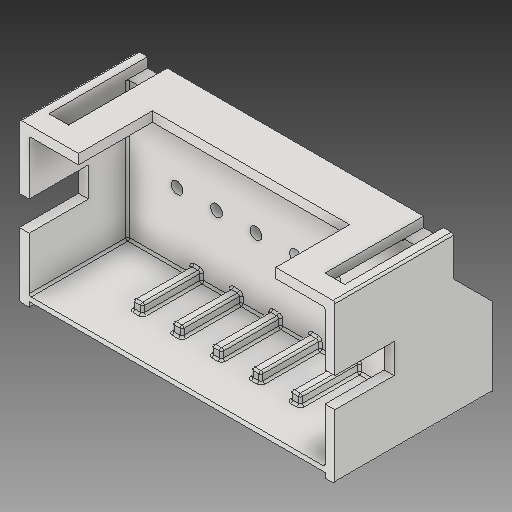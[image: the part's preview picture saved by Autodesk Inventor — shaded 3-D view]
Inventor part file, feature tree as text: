
AUTODESK INVENTOR PART (.ipt)
format: ipt  version: 2019 (Build 230136000, 136)  size: 262,656 bytes
history: mixed  units: mm
features: other x1, fillet x1, imported_body x1
ambient origin geometry x8: Origin, YZ Plane, XZ Plane, XY Plane, X Axis, Y Axis, Z Axis, Center Point
bodies: Body1 (imported_parasolid)
feature tree (3):
  other  "Твердое тело1"
  fillet  "Fillet1"  [1 undecoded]
  imported_body  NMx_Import_Brep_tag  [imported B-rep: ~180 faces, bbox_mm=[16.0, 8.0, 8.0]]
note: 1 required parameter value undecoded (feature->parameter linkage not recoverable at this tier; creation-order binding heuristic only, values carry confidence <= 0.55)
